# Revit family: Magnuson-DS-Wall-Coat_Rack
name_source: partatom
category: Furniture
revit_build: Autodesk Revit 2014 (Build: 20130308_1515(x64)
units: mm (PartAtom-declared; Revit-internal decimal feet)

## types (5) — shared parameters
Assembly Code = E2020200
Frame = MG - Steel, Wrought
Hanger Rod = MG - Black Plastic
Keynote = 12500
Low Emitting Finish = Yes
Low Emitting Material = Yes
Manufacturer = Magnuson Group
Salvage or Reuse = Yes
Shelf = MG - Steel, Wrought
Type Comments = DS Rack
URL = www.magnusongroup.com
zero-valued in all types: Percentage of Recycled Content

## per-type parameters (varying)
| type | # Support | Description | Width |
| 3D-DS-3H | 2 | 36W Wall Mounted Rack | 36" |
| 3D-DS-4H | 2 | 48W Wall Mounted Rack | 48" |
| 3D-DS-2H | 2 | 24W Wall Mounted Rack | 24" |
| 3D-DS-5H | 3 | 60W Wall Mounted Rack | 60" |
| 3D-DS-6H | 3 | 72W Wall Mounted Rack | 72" |

note: column(s) folded — value = type name in every type: Model

## geometry (parser evidence)
native form markers: Sweep x1
no freeform markers — native parametric forms only
